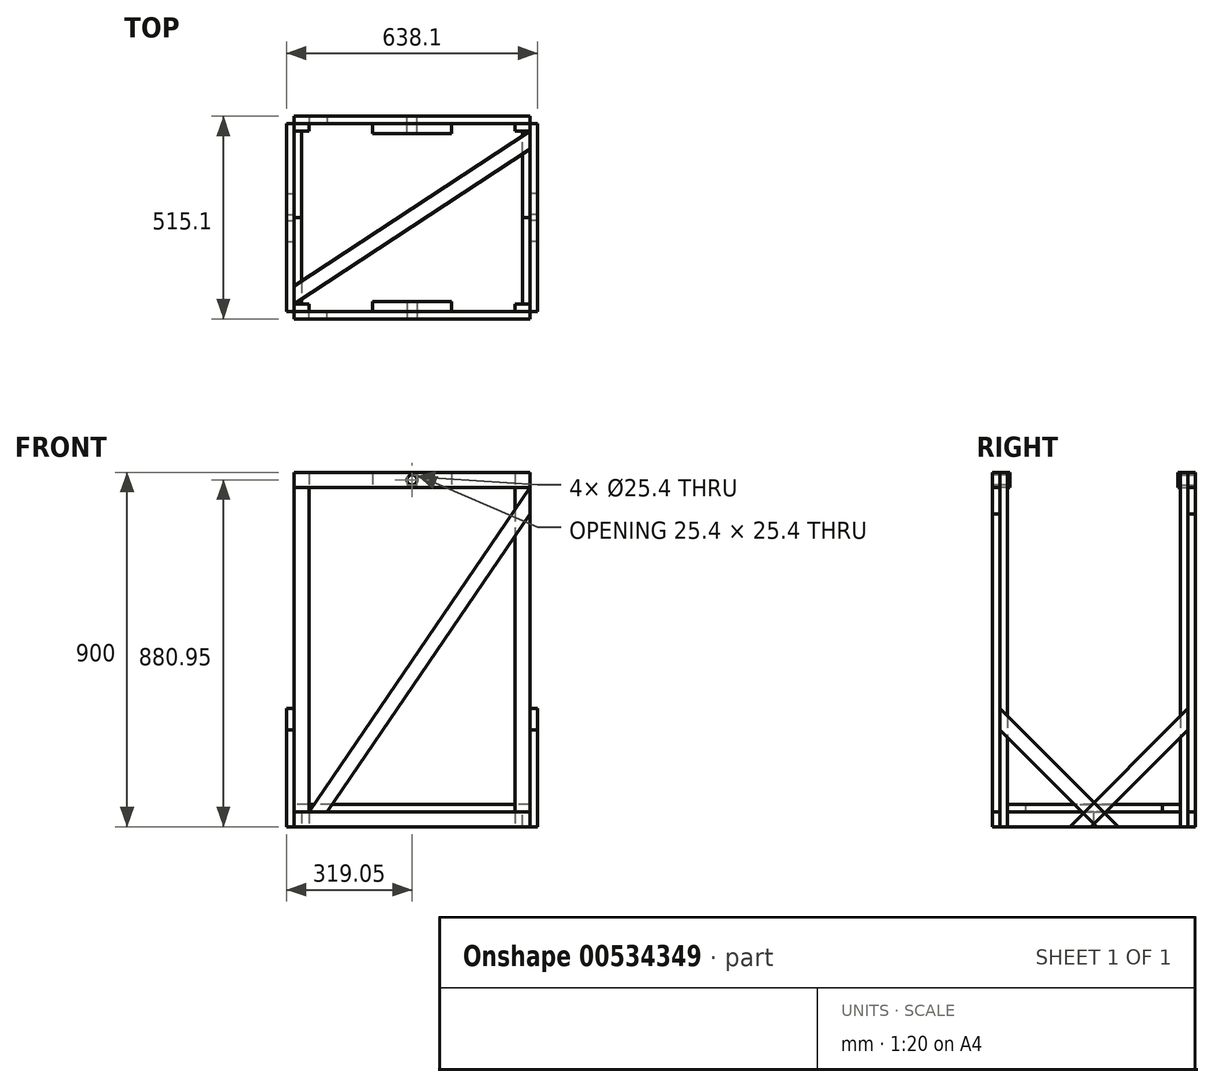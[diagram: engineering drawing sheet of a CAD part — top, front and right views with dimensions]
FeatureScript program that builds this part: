
annotation { "Feature Type Name" : "Feature", "Feature Type Description" : "" }
export const myFeature = defineFeature(function(context is Context, id is Id, definition is map)
    precondition{}
    {
        {
            var Q0;
            Q0=qCreatedBy(makeId("Front.planeOp"),FACE);
            var sketch = newSketch(context, id + "F0", { "sketchPlane" : qUnion([Q0])});
            skLineSegment(sketch, "E0", {"start": v(0, 900) * mm, "end": v(-300, 0) * mm, "construction": true});
            skLineSegment(sketch, "E1", {"start": v(-300, 0) * mm, "end": v(300, 0) * mm, "construction": true});
            skLineSegment(sketch, "E2", {"start": v(300, 0) * mm, "end": v(0, 900) * mm, "construction": true});
            skLineSegment(sketch, "E3", {"start": v(0, 900) * mm, "end": v(0, 0) * mm, "construction": true});
            skLineSegment(sketch, "E4", {"start": v(-287.3, 38.1) * mm, "end": v(287.3, 38.1) * mm, "construction": true});
            skLineSegment(sketch, "E5", {"start": v(-20.08, 839.76) * mm, "end": v(259.84, 0) * mm, "construction": true});
            skLineSegment(sketch, "E6", {"start": v(20.08, 839.76) * mm, "end": v(-259.84, 0) * mm, "construction": true});
            skLineSegment(sketch, "E7", {"start": v(-300, 0) * mm, "end": v(300, 0) * mm});
            skLineSegment(sketch, "E8", {"start": v(300, 0) * mm, "end": v(300, 38.1) * mm});
            skLineSegment(sketch, "E9", {"start": v(300, 38.1) * mm, "end": v(-300, 38.1) * mm});
            skLineSegment(sketch, "E10", {"start": v(-300, 38.1) * mm, "end": v(-300, 0) * mm});
            skLineSegment(sketch, "E11.bottom", {"start": v(-300, 38.1) * mm, "end": v(-261.9, 38.1) * mm});
            skLineSegment(sketch, "E11.top", {"start": v(-300, 900) * mm, "end": v(-261.9, 900) * mm});
            skLineSegment(sketch, "E11.left", {"start": v(-300, 38.1) * mm, "end": v(-300, 900) * mm});
            skLineSegment(sketch, "E11.right", {"start": v(-261.9, 38.1) * mm, "end": v(-261.9, 900) * mm});
            skLineSegment(sketch, "E12.bottom", {"start": v(300, 38.1) * mm, "end": v(261.9, 38.1) * mm});
            skLineSegment(sketch, "E12.top", {"start": v(300, 900) * mm, "end": v(261.9, 900) * mm});
            skLineSegment(sketch, "E12.left", {"start": v(300, 38.1) * mm, "end": v(300, 900) * mm});
            skLineSegment(sketch, "E12.right", {"start": v(261.9, 38.1) * mm, "end": v(261.9, 900) * mm});
            skLineSegment(sketch, "E13.bottom", {"start": v(-261.9, 900) * mm, "end": v(261.9, 900) * mm});
            skLineSegment(sketch, "E13.top", {"start": v(-261.9, 861.9) * mm, "end": v(261.9, 861.9) * mm});
            skLineSegment(sketch, "E13.left", {"start": v(-261.9, 900) * mm, "end": v(-261.9, 861.9) * mm});
            skLineSegment(sketch, "E13.right", {"start": v(261.9, 900) * mm, "end": v(261.9, 861.9) * mm});
            skLineSegment(sketch, "E14", {"start": v(-261.9, 861.9) * mm, "end": v(-300, 861.9) * mm});
            skLineSegment(sketch, "E15", {"start": v(261.9, 861.9) * mm, "end": v(300, 861.9) * mm});
            skSolve(sketch);
        }
        {
            var Q0;
            {var subQ0=sQuery(id+"F0.wireOp",EDGE,"E11.top");Q0=makeQuery(id+"F0.imprint","IMPRINT",FACE,{"disambiguationData":[TD([[makeQuery(id+"F0.imprint","IMPRINT",EDGE,{"derivedFrom":subQ0}),-1.0]])]});}
            var Q1;
            Q1=makeQuery(id+"F0.imprint","IMPRINT",FACE,{"disambiguationData":[TD([[makeQuery(id+"F0.imprint","IMPRINT",EDGE,{"derivedFrom":sQuery(id+"F0.wireOp",EDGE,"E13.bottom")}),-1.0]])]});
            var Q2;
            {var subQ0=sQuery(id+"F0.wireOp",EDGE,"E12.top");Q2=makeQuery(id+"F0.imprint","IMPRINT",FACE,{"disambiguationData":[TD([[makeQuery(id+"F0.imprint","IMPRINT",EDGE,{"derivedFrom":subQ0}),1.0]])]});}
            var Q3;
            Q3=makeQuery(id+"F0.imprint","IMPRINT",FACE,{"disambiguationData":[TD([[makeQuery(id+"F0.imprint","IMPRINT",EDGE,{"derivedFrom":sQuery(id+"F0.wireOp",EDGE,"E7")}),1.0]])]});
            extrude(context, id + "F1", {"entities" : qUnion([Q0, Q1, Q2, Q3]), "oppositeDirection" : true, "depth" : 19.05 * mm, "offsetDistance" : 25 * mm});
        }
        {
            var Q0;
            Q0=makeQuery(id+"F1.opExtrude","CAP_FACE",FACE,{"disambiguationData":[OSD([sQuery(id+"F0.wireOp",EDGE,"E11.top"),sQuery(id+"F0.wireOp",EDGE,"E11.left"),sQuery(id+"F0.wireOp",EDGE,"E12.top"),sQuery(id+"F0.wireOp",EDGE,"E12.left"),sQuery(id+"F0.wireOp",EDGE,"E13.bottom"),sQuery(id+"F0.wireOp",EDGE,"E13.top"),sQuery(id+"F0.wireOp",EDGE,"E14"),sQuery(id+"F0.wireOp",EDGE,"E15")])],"isStart":true});
            var sketch = newSketch(context, id + "F2", { "sketchPlane" : qUnion([Q0])});
            skLineSegment(sketch, "E16.bottom", {"start": v(-300, 900) * mm, "end": v(-261.9, 900) * mm});
            skLineSegment(sketch, "E16.top", {"start": v(-300, 0) * mm, "end": v(-261.9, 0) * mm});
            skLineSegment(sketch, "E16.left", {"start": v(-300, 900) * mm, "end": v(-300, 0) * mm});
            skLineSegment(sketch, "E16.right", {"start": v(-261.9, 900) * mm, "end": v(-261.9, 0) * mm});
            skLineSegment(sketch, "E17.bottom", {"start": v(300, 900) * mm, "end": v(261.9, 900) * mm});
            skLineSegment(sketch, "E17.top", {"start": v(300, 0) * mm, "end": v(261.9, 0) * mm});
            skLineSegment(sketch, "E17.left", {"start": v(300, 900) * mm, "end": v(300, 0) * mm});
            skLineSegment(sketch, "E17.right", {"start": v(261.9, 900) * mm, "end": v(261.9, 0) * mm});
            skSolve(sketch);
        }
        {
            var Q0;
            {var subQ0=sQuery(id+"F2.wireOp",EDGE,"E16.top");Q0=makeQuery(id+"F2.imprint","IMPRINT",FACE,{"disambiguationData":[TD([[makeQuery(id+"F2.imprint","IMPRINT",EDGE,{"derivedFrom":subQ0}),1.0]])]});}
            var Q1;
            {var subQ0=sQuery(id+"F2.wireOp",EDGE,"E16.bottom");Q1=makeQuery(id+"F2.imprint","IMPRINT",FACE,{"disambiguationData":[TD([[makeQuery(id+"F2.imprint","IMPRINT",EDGE,{"derivedFrom":subQ0}),-1.0]])]});}
            var Q2;
            {var subQ0=sQuery(id+"F2.wireOp",EDGE,"E17.top");Q2=makeQuery(id+"F2.imprint","IMPRINT",FACE,{"disambiguationData":[TD([[makeQuery(id+"F2.imprint","IMPRINT",EDGE,{"derivedFrom":subQ0}),-1.0]])]});}
            var Q3;
            {var subQ0=sQuery(id+"F2.wireOp",EDGE,"E17.bottom");Q3=makeQuery(id+"F2.imprint","IMPRINT",FACE,{"disambiguationData":[TD([[makeQuery(id+"F2.imprint","IMPRINT",EDGE,{"derivedFrom":subQ0}),-1.0]])]});}
            extrude(context, id + "F3", {"entities" : qUnion([Q0, Q1, Q2, Q3]), "depth" : 19.05 * mm, "offsetDistance" : 25 * mm});
        }
        {
            var Q0;
            Q0=makeQuery(id+"F3.opExtrude","CAP_FACE",FACE,{"disambiguationData":[OSD([sQuery(id+"F2.wireOp",EDGE,"E17.bottom"),sQuery(id+"F2.wireOp",EDGE,"E17.top"),sQuery(id+"F2.wireOp",EDGE,"E17.left"),sQuery(id+"F2.wireOp",EDGE,"E17.right")])],"isStart":true});
            var sketch = newSketch(context, id + "F4", { "sketchPlane" : qUnion([Q0])});
            skLineSegment(sketch, "E18", {"start": v(-300, 861.9) * mm, "end": v(-300, 794.29) * mm});
            skLineSegment(sketch, "E19", {"start": v(-300, 794.29) * mm, "end": v(215.78, 38.1) * mm});
            skLineSegment(sketch, "E20", {"start": v(261.9, 38.1) * mm, "end": v(-300, 861.9) * mm});
            skLineSegment(sketch, "E21", {"start": v(215.78, 38.1) * mm, "end": v(261.9, 38.1) * mm});
            skSolve(sketch);
        }
        {
            var Q0;
            {var subQ0=sQuery(id+"F4.wireOp",EDGE,"E18");Q0=makeQuery(id+"F4.imprint","IMPRINT",FACE,{"disambiguationData":[TD([[makeQuery(id+"F4.imprint","IMPRINT",EDGE,{"derivedFrom":subQ0}),1.0]])]});}
            var Q1;
            {var subQ0=sQuery(id+"F4.wireOp",EDGE,"E21");Q1=makeQuery(id+"F4.imprint","IMPRINT",FACE,{"disambiguationData":[TD([[makeQuery(id+"F4.imprint","IMPRINT",EDGE,{"derivedFrom":subQ0}),1.0]])]});}
            extrude(context, id + "F5", {"entities" : qUnion([Q0, Q1]), "depth" : 19.05 * mm, "offsetDistance" : 25 * mm});
        }
        {
            var Q0;
            Q0=makeQuery(id+"F1.opExtrude","CAP_FACE",FACE,{"disambiguationData":[OSD([sQuery(id+"F0.wireOp",EDGE,"E11.top"),sQuery(id+"F0.wireOp",EDGE,"E11.left"),sQuery(id+"F0.wireOp",EDGE,"E12.top"),sQuery(id+"F0.wireOp",EDGE,"E12.left"),sQuery(id+"F0.wireOp",EDGE,"E13.bottom"),sQuery(id+"F0.wireOp",EDGE,"E13.top"),sQuery(id+"F0.wireOp",EDGE,"E14"),sQuery(id+"F0.wireOp",EDGE,"E15")])],"isStart":false});
            var sketch = newSketch(context, id + "F6", { "sketchPlane" : qUnion([Q0])});
            skCircle(sketch, "E22", {"center": v(0, 880.95) * mm, "radius": 12.7 * mm});
            skSolve(sketch);
        }
        {
            var Q0;
            Q0=makeQuery(id+"F6.imprint","IMPRINT",FACE,{"disambiguationData":[TD([[makeQuery(id+"F6.imprint","IMPRINT",EDGE,{"derivedFrom":sQuery(id+"F6.wireOp",EDGE,"E22")}),1.0]])]});
            extrude(context, id + "F7", {"entities" : qUnion([Q0]), "operationType" : NewBodyOperationType.REMOVE, "oppositeDirection" : true, "depth" : 25 * mm, "offsetDistance" : 25 * mm});
        }
        {
            var Q0;
            Q0=makeQuery(id+"F3.opExtrude","CAP_FACE",FACE,{"disambiguationData":[OSD([sQuery(id+"F2.wireOp",EDGE,"E16.bottom"),sQuery(id+"F2.wireOp",EDGE,"E16.top"),sQuery(id+"F2.wireOp",EDGE,"E16.left"),sQuery(id+"F2.wireOp",EDGE,"E16.right")])],"isStart":false});
            var sketch = newSketch(context, id + "F8", { "sketchPlane" : qUnion([Q0])});
            skLineSegment(sketch, "E23.bottom", {"start": v(-300, 38.1) * mm, "end": v(-280.95, 38.1) * mm});
            skLineSegment(sketch, "E23.top", {"start": v(-300, 0) * mm, "end": v(-280.95, 0) * mm});
            skLineSegment(sketch, "E23.left", {"start": v(-300, 38.1) * mm, "end": v(-300, 0) * mm});
            skLineSegment(sketch, "E23.right", {"start": v(-280.95, 38.1) * mm, "end": v(-280.95, 0) * mm});
            skLineSegment(sketch, "E24.bottom", {"start": v(280.95, 0) * mm, "end": v(300, 0) * mm});
            skLineSegment(sketch, "E24.top", {"start": v(280.95, 38.1) * mm, "end": v(300, 38.1) * mm});
            skLineSegment(sketch, "E24.left", {"start": v(280.95, 0) * mm, "end": v(280.95, 38.1) * mm});
            skLineSegment(sketch, "E24.right", {"start": v(300, 0) * mm, "end": v(300, 38.1) * mm});
            skSolve(sketch);
        }
        {
            var Q0;
            Q0=makeQuery(id+"F8.imprint","IMPRINT",FACE,{"disambiguationData":[TD([[makeQuery(id+"F8.imprint","IMPRINT",EDGE,{"derivedFrom":sQuery(id+"F8.wireOp",EDGE,"E23.bottom")}),-1.0]])]});
            var Q1;
            Q1=makeQuery(id+"F8.imprint","IMPRINT",FACE,{"disambiguationData":[TD([[makeQuery(id+"F8.imprint","IMPRINT",EDGE,{"derivedFrom":sQuery(id+"F8.wireOp",EDGE,"E24.bottom")}),1.0]])]});
            extrude(context, id + "F9", {"entities" : qUnion([Q0, Q1]), "depth" : (213.1 + 6.35) * mm, "offsetDistance" : 25 * mm});
        }
        {
            var Q0;
            Q0=makeQuery(id+"F3.opExtrude","SWEPT_FACE",FACE,{"disambiguationData":[OSD([sQuery(id+"F2.wireOp",EDGE,"E16.left")])]});
            var sketch = newSketch(context, id + "F10", { "sketchPlane" : qUnion([Q0])});
            skLineSegment(sketch, "E25", {"start": v(0, 300) * mm, "end": v(0, 246.12) * mm});
            skLineSegment(sketch, "E26", {"start": v(0, 246.12) * mm, "end": v(246.12, 0) * mm});
            skLineSegment(sketch, "E27", {"start": v(246.12, 0) * mm, "end": v(300, 0) * mm});
            skLineSegment(sketch, "E28", {"start": v(300, 0) * mm, "end": v(0, 300) * mm});
            skSolve(sketch);
        }
        {
            var Q0;
            {var subQ0=sQuery(id+"F10.wireOp",EDGE,"E27");Q0=makeQuery(id+"F10.imprint","IMPRINT",FACE,{"disambiguationData":[TD([[makeQuery(id+"F10.imprint","IMPRINT",EDGE,{"derivedFrom":subQ0}),1.0]])]});}
            var Q1;
            {var subQ0=sQuery(id+"F10.wireOp",EDGE,"E25");Q1=makeQuery(id+"F10.imprint","IMPRINT",FACE,{"disambiguationData":[TD([[makeQuery(id+"F10.imprint","IMPRINT",EDGE,{"derivedFrom":subQ0}),1.0]])]});}
            extrude(context, id + "F11", {"entities" : qUnion([Q0, Q1]), "depth" : 19.05 * mm, "offsetDistance" : 25 * mm});
        }
        {
            var Q0;
            Q0=makeQuery(id+"F1.opExtrude","CAP_FACE",FACE,{"disambiguationData":[OSD([sQuery(id+"F0.wireOp",EDGE,"E11.top"),sQuery(id+"F0.wireOp",EDGE,"E11.left"),sQuery(id+"F0.wireOp",EDGE,"E12.top"),sQuery(id+"F0.wireOp",EDGE,"E12.left"),sQuery(id+"F0.wireOp",EDGE,"E13.bottom"),sQuery(id+"F0.wireOp",EDGE,"E13.top"),sQuery(id+"F0.wireOp",EDGE,"E14"),sQuery(id+"F0.wireOp",EDGE,"E15")])],"isStart":true});
            var sketch = newSketch(context, id + "F12", { "sketchPlane" : qUnion([Q0])});
            skLineSegment(sketch, "E29.bottom", {"start": v(-100, 900) * mm, "end": v(100, 900) * mm});
            skLineSegment(sketch, "E29.top", {"start": v(-100, 861.9) * mm, "end": v(100, 861.9) * mm});
            skLineSegment(sketch, "E29.left", {"start": v(-100, 900) * mm, "end": v(-100, 861.9) * mm});
            skLineSegment(sketch, "E29.right", {"start": v(100, 900) * mm, "end": v(100, 861.9) * mm});
            skSolve(sketch);
        }
        {
            var Q0;
            Q0=makeQuery(id+"F12.imprint","IMPRINT",FACE,{"disambiguationData":[TD([[makeQuery(id+"F12.imprint","IMPRINT",EDGE,{"derivedFrom":sQuery(id+"F12.wireOp",EDGE,"E29.bottom")}),-1.0]])]});
            extrude(context, id + "F13", {"entities" : qUnion([Q0]), "depth" : 25.4 * mm, "offsetDistance" : 25 * mm});
        }
        {
            var Q0;
            Q0=makeQuery(id+"F11.opExtrude","SWEPT_BODY",BODY,{"disambiguationData":[OSD([sQuery(id+"F10.wireOp",EDGE,"E25"),sQuery(id+"F10.wireOp",EDGE,"E26"),sQuery(id+"F10.wireOp",EDGE,"E27"),sQuery(id+"F10.wireOp",EDGE,"E28")])]});
            var Q1;
            Q1=qCreatedBy(makeId("Right.planeOp"),FACE);
            mirror(context, id + "F14", {"entities" : qUnion([Q0]), "mirrorPlane" : qUnion([Q1])});
        }
        {
            var Q0;
            Q0=makeQuery(id+"F1.opExtrude","SWEPT_BODY",BODY,{"disambiguationData":[OSD([sQuery(id+"F0.wireOp",EDGE,"E7"),sQuery(id+"F0.wireOp",EDGE,"E8"),sQuery(id+"F0.wireOp",EDGE,"E9"),sQuery(id+"F0.wireOp",EDGE,"E10"),sQuery(id+"F0.wireOp",EDGE,"E11.bottom"),sQuery(id+"F0.wireOp",EDGE,"E12.bottom")])]});
            var Q1;
            Q1=makeQuery(id+"F1.opExtrude","SWEPT_BODY",BODY,{"disambiguationData":[OSD([sQuery(id+"F0.wireOp",EDGE,"E11.top"),sQuery(id+"F0.wireOp",EDGE,"E11.left"),sQuery(id+"F0.wireOp",EDGE,"E12.top"),sQuery(id+"F0.wireOp",EDGE,"E12.left"),sQuery(id+"F0.wireOp",EDGE,"E13.bottom"),sQuery(id+"F0.wireOp",EDGE,"E13.top"),sQuery(id+"F0.wireOp",EDGE,"E14"),sQuery(id+"F0.wireOp",EDGE,"E15")])]});
            var Q2;
            Q2=makeQuery(id+"F3.opExtrude","SWEPT_BODY",BODY,{"disambiguationData":[OSD([sQuery(id+"F2.wireOp",EDGE,"E16.bottom"),sQuery(id+"F2.wireOp",EDGE,"E16.top"),sQuery(id+"F2.wireOp",EDGE,"E16.left"),sQuery(id+"F2.wireOp",EDGE,"E16.right")])]});
            var Q3;
            Q3=makeQuery(id+"F3.opExtrude","SWEPT_BODY",BODY,{"disambiguationData":[OSD([sQuery(id+"F2.wireOp",EDGE,"E17.bottom"),sQuery(id+"F2.wireOp",EDGE,"E17.top"),sQuery(id+"F2.wireOp",EDGE,"E17.left"),sQuery(id+"F2.wireOp",EDGE,"E17.right")])]});
            var Q4;
            Q4=makeQuery(id+"F5.opExtrude","SWEPT_BODY",BODY,{"disambiguationData":[OSD([sQuery(id+"F4.wireOp",EDGE,"E18"),sQuery(id+"F4.wireOp",EDGE,"E19"),sQuery(id+"F4.wireOp",EDGE,"E20"),sQuery(id+"F4.wireOp",EDGE,"E21")])]});
            var Q5;
            Q5=makeQuery(id+"F9.opExtrude","SWEPT_BODY",BODY,{"disambiguationData":[OSD([sQuery(id+"F8.wireOp",EDGE,"E23.bottom"),sQuery(id+"F8.wireOp",EDGE,"E23.top"),sQuery(id+"F8.wireOp",EDGE,"E23.left"),sQuery(id+"F8.wireOp",EDGE,"E23.right")])]});
            var Q6;
            Q6=makeQuery(id+"F9.opExtrude","SWEPT_BODY",BODY,{"disambiguationData":[OSD([sQuery(id+"F8.wireOp",EDGE,"E24.bottom"),sQuery(id+"F8.wireOp",EDGE,"E24.top"),sQuery(id+"F8.wireOp",EDGE,"E24.left"),sQuery(id+"F8.wireOp",EDGE,"E24.right")])]});
            var Q7;
            Q7=makeQuery(id+"F11.opExtrude","SWEPT_BODY",BODY,{"disambiguationData":[OSD([sQuery(id+"F10.wireOp",EDGE,"E25"),sQuery(id+"F10.wireOp",EDGE,"E26"),sQuery(id+"F10.wireOp",EDGE,"E27"),sQuery(id+"F10.wireOp",EDGE,"E28")])]});
            var Q8;
            Q8=makeQuery(id+"F14.opPattern","COPY",BODY,{"derivedFrom":makeQuery(id+"F11.opExtrude","SWEPT_BODY",BODY,{"disambiguationData":[OSD([sQuery(id+"F10.wireOp",EDGE,"E25"),sQuery(id+"F10.wireOp",EDGE,"E26"),sQuery(id+"F10.wireOp",EDGE,"E27"),sQuery(id+"F10.wireOp",EDGE,"E28")])]}),"instanceName":"1"});
            var Q9;
            Q9=makeQuery(id+"F13.opExtrude","SWEPT_BODY",BODY,{"disambiguationData":[OSD([sQuery(id+"F0.wireOp",EDGE,"E11.top"),sQuery(id+"F0.wireOp",EDGE,"E11.left"),sQuery(id+"F0.wireOp",EDGE,"E12.top"),sQuery(id+"F0.wireOp",EDGE,"E12.left"),sQuery(id+"F0.wireOp",EDGE,"E13.bottom"),sQuery(id+"F0.wireOp",EDGE,"E13.top"),sQuery(id+"F0.wireOp",EDGE,"E14"),sQuery(id+"F0.wireOp",EDGE,"E15"),sQuery(id+"F6.wireOp",EDGE,"E22"),sQuery(id+"F12.wireOp",EDGE,"E29.bottom"),sQuery(id+"F12.wireOp",EDGE,"E29.top"),sQuery(id+"F12.wireOp",EDGE,"E29.left"),sQuery(id+"F12.wireOp",EDGE,"E29.right")])]});
            var Q10;
            Q10=makeQuery(id+"F9.opExtrude","CAP_FACE",FACE,{"disambiguationData":[OSD([sQuery(id+"F8.wireOp",EDGE,"E23.bottom"),sQuery(id+"F8.wireOp",EDGE,"E23.top"),sQuery(id+"F8.wireOp",EDGE,"E23.left"),sQuery(id+"F8.wireOp",EDGE,"E23.right")])],"isStart":false});
            mirror(context, id + "F15", {"entities" : qUnion([Q0, Q1, Q2, Q3, Q4, Q5, Q6, Q7, Q8, Q9]), "mirrorPlane" : qUnion([Q10])});
        }
        {
            var Q0;
            Q0=makeQuery(id+"F9.opExtrude","SWEPT_FACE",FACE,{"disambiguationData":[OSD([sQuery(id+"F8.wireOp",EDGE,"E24.top")])]});
            var sketch = newSketch(context, id + "F16", { "sketchPlane" : qUnion([Q0])});
            skLineSegment(sketch, "E30", {"start": v(300, -19.05) * mm, "end": v(300, -64.6) * mm});
            skLineSegment(sketch, "E31", {"start": v(300, -64.6) * mm, "end": v(-300, -457.95) * mm});
            skLineSegment(sketch, "E32", {"start": v(-300, -457.95) * mm, "end": v(-300, -412.4) * mm});
            skLineSegment(sketch, "E33", {"start": v(-300, -412.4) * mm, "end": v(300, -19.05) * mm});
            skSolve(sketch);
        }
        {
            var Q0;
            {var subQ0=sQuery(id+"F16.wireOp",EDGE,"E32");Q0=makeQuery(id+"F16.imprint","IMPRINT",FACE,{"disambiguationData":[TD([[makeQuery(id+"F16.imprint","IMPRINT",EDGE,{"derivedFrom":subQ0}),-1.0]])]});}
            var Q1;
            {var subQ0=sQuery(id+"F16.wireOp",EDGE,"E30");Q1=makeQuery(id+"F16.imprint","IMPRINT",FACE,{"disambiguationData":[TD([[makeQuery(id+"F16.imprint","IMPRINT",EDGE,{"derivedFrom":subQ0}),1.0]])]});}
            extrude(context, id + "F17", {"entities" : qUnion([Q0, Q1]), "depth" : 19.05 * mm, "offsetDistance" : 25 * mm});
        }
    });
